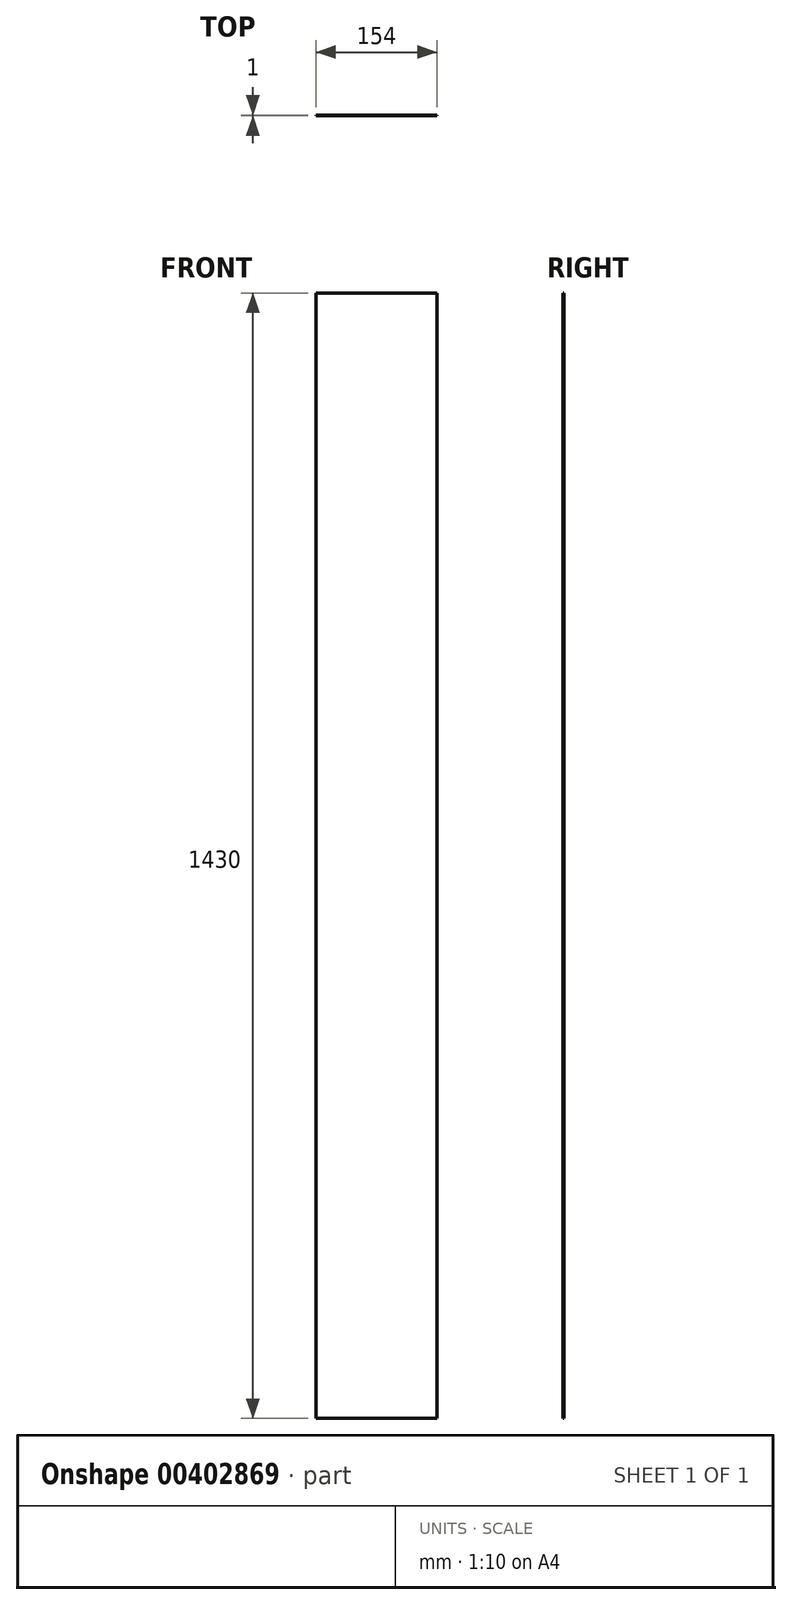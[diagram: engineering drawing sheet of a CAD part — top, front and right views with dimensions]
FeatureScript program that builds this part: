
annotation { "Feature Type Name" : "Feature", "Feature Type Description" : "" }
export const myFeature = defineFeature(function(context is Context, id is Id, definition is map)
    precondition{}
    {
        {
            var Q0;
            Q0=qCreatedBy(makeId("Front.planeOp"),FACE);
            var sketch = newSketch(context, id + "F0", { "sketchPlane" : qUnion([Q0])});
            skLineSegment(sketch, "E0.bottom", {"start": v(-77, 715) * mm, "end": v(77, 715) * mm});
            skLineSegment(sketch, "E0.top", {"start": v(-77, -715) * mm, "end": v(77, -715) * mm});
            skLineSegment(sketch, "E0.left", {"start": v(-77, 715) * mm, "end": v(-77, -715) * mm});
            skLineSegment(sketch, "E0.right", {"start": v(77, 715) * mm, "end": v(77, -715) * mm});
            skPoint(sketch, "E0.middle", {"position": v(0, 0) * mm});
            skSolve(sketch);
        }
        {
            var Q0;
            Q0=makeQuery(id+"F0.imprint","IMPRINT",FACE,{"disambiguationData":[TD([[makeQuery(id+"F0.imprint","IMPRINT",EDGE,{"derivedFrom":sQuery(id+"F0.wireOp",EDGE,"E0.bottom")}),-1.0]])]});
            extrude(context, id + "F1", {"entities" : qUnion([Q0]), "depth" : 1 * mm});
        }
    });
